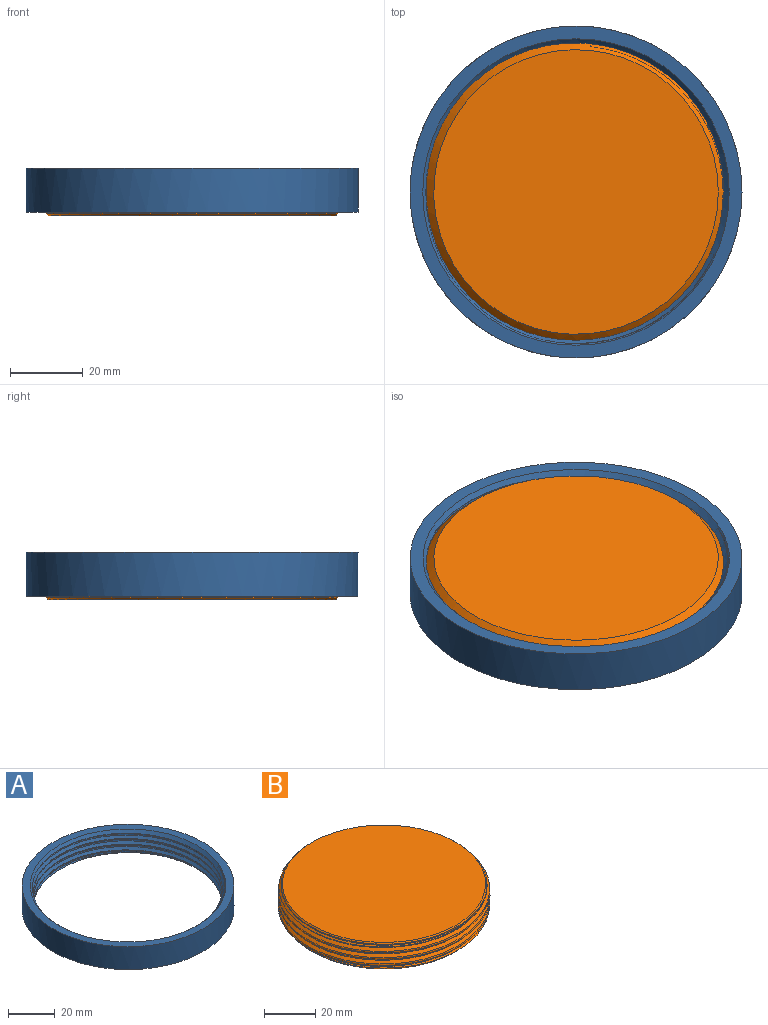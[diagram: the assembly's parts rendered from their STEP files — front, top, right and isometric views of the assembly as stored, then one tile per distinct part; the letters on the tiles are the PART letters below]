
ASSEMBLY  parts=2 mates=1
PART A: 8 faces, bbox 91.9x97.3x15.5 mm
  f0: bspline ~95.95x83.09mm, area 1401.7mm2, adj f1,f3,f4,f7
  f1: bspline ~96.43x83.51mm, area 790.7mm2, adj f0,f2,f4,f7
  f2: bspline ~95.95x83.09mm, area 1402.1mm2, adj f1,f3,f4,f7
  f3: cylinder r=40.5mm len=81mm, axis (0,0,1), area 167.3mm2, adj f0,f2,f4,f7
  f4: plane 91.91x91.91mm, normal (0,0,-1), area 1187.4mm2, adj f0,f1,f2,f3,f6
  f5: plane 91x91mm, normal (0,0,1), area 962.1mm2, adj f6,f7
  f6: cylinder r=45.5mm len=91mm, axis (0,0,1), area 3430.6mm2, adj f4,f5
  f7: cone r=42mm half-angle=45deg, axis (0,0,1), area 328mm2, adj f0,f1,f2,f3,f5
PART B: 13 faces, bbox 82.5x95.3x13.8 mm
  f0: cylinder r=40mm len=80mm, axis (0,0,-1), area 149mm2, adj f4,f5,f7,f11,f12
  f1: cylinder r=40mm len=39.8mm, axis (0,0,-1), area 10.1mm2, adj f2,f5,f7,f8
  f2: cylinder r=40mm len=80mm, axis (0,0,-1), area 50.2mm2, adj f1,f3,f5,f7
  f3: cylinder r=40mm len=80mm, axis (0,0,-1), area 50.2mm2, adj f2,f4,f5,f7
  f4: cylinder r=40mm len=80mm, axis (0,0,-1), area 50.2mm2, adj f0,f3,f5,f7
  f5: bspline ~94.79x82.09mm, area 1249mm2, adj f0,f1,f2,f3,f4,f6,f8,f11
  f6: bspline ~95.27x82.51mm, area 602.4mm2, adj f5,f7,f8,f11
  f7: bspline ~94.79x82.09mm, area 1249.9mm2, adj f0,f1,f2,f3,f4,f6,f8,f11
  f8: cone r=43mm half-angle=45deg, axis (0,0,1), area 570.1mm2, adj f1,f5,f6,f7,f9
  f9: plane 78x78mm, normal (0,0,-1), area 4778.4mm2, adj f8
  f10: plane 79x79mm, normal (0,0,1), area 4901.7mm2, adj f12
  f11: cone r=49.71mm half-angle=45deg, axis (0,0,-1), area 219.7mm2, adj f0,f5,f6,f7
  f12: cone r=39.5mm half-angle=45deg, axis (0,0,-1), area 176.6mm2, adj f0,f10
PLACE A t=(-18.12,7.08,17.46)mm
PLACE B rot(axis=(0,1,0),180deg) t=(-18.12,7.08,-2.54)mm
MATE fastened B.f0 <-> A.f3  axis (0,0,1) through (-18.12,7.08,-8.54)mm
